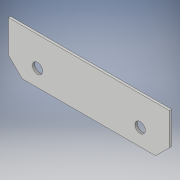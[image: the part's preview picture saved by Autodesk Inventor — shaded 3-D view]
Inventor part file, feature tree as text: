
AUTODESK INVENTOR PART (.ipt)
format: ipt  version: 2017 (Build 210142000, 142)  size: 119,808 bytes
history: native  units: in
note: dims shown in document units (in); Inventor stores cm internally (conversion verified against a paired STEP export)
features: extrude x3, sketch x3
ambient origin geometry x8: Origin, YZ Plane, XZ Plane, XY Plane, X Axis, Y Axis, Z Axis, Center Point
bodies: Solid1 (feature_tree)
feature tree (6):
  extrude  "Extrusion1"  Depth=5.0in
  extrude  "Extrusion2"  Depth=0.25in TaperAngle=0.0deg
  sketch  "Sketch3"  dims[d10=1.124in d14=2.0in d15=0.0in d18=1.124in d19=1.5in d20=180.0deg d31=1.7in d32=1.7in]
  extrude  "Extrusion3"  Depth=2.0in TaperAngle=0.0deg
  sketch  "Sketch1"  dims[d0=17.5in d1=5.0in]
  sketch  "Sketch2"  dims[d2=0.25in d3=0.0in d4=2.0in d5=0.0in]
